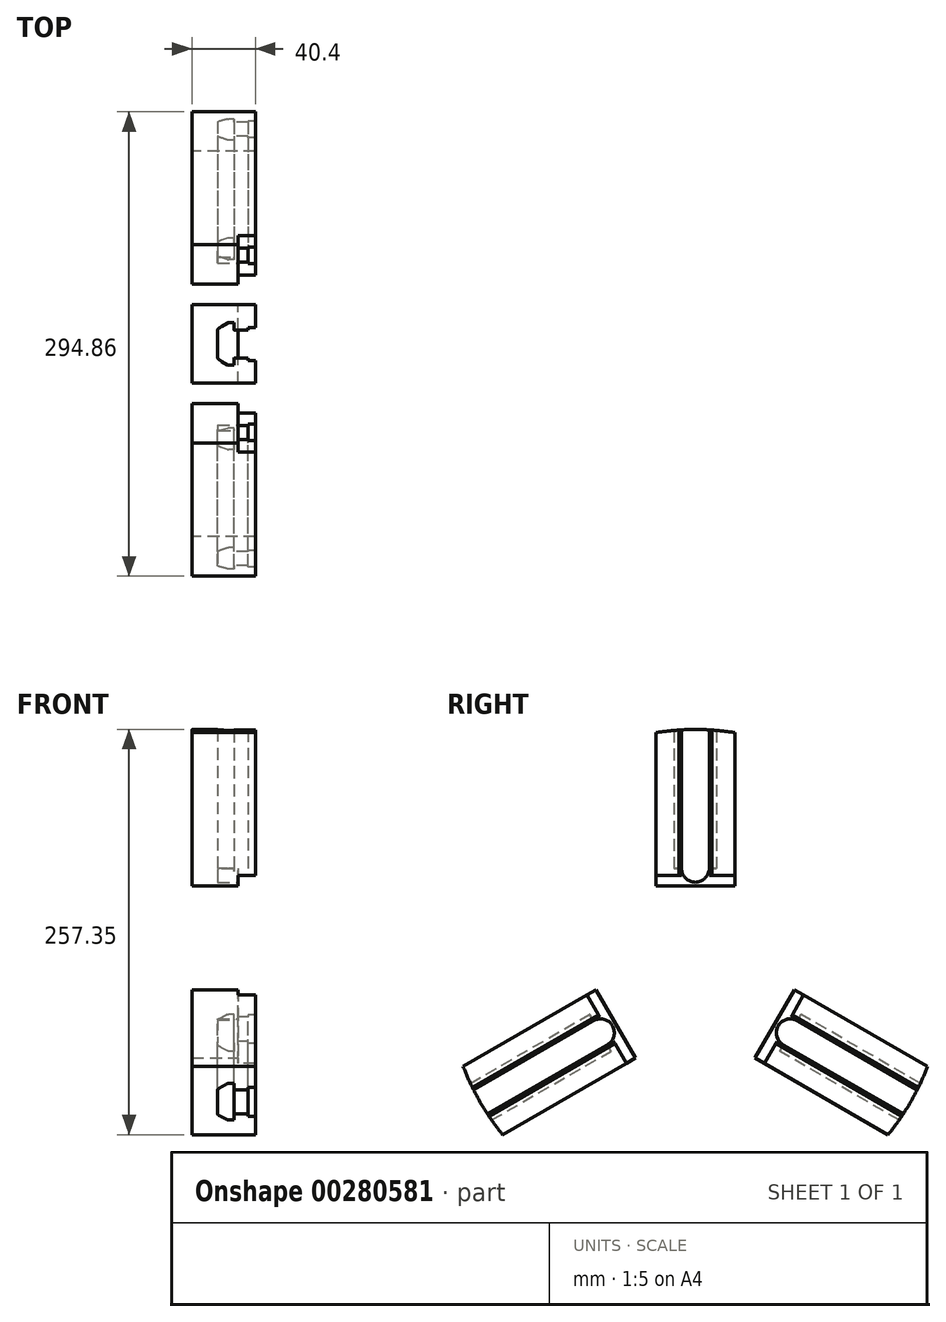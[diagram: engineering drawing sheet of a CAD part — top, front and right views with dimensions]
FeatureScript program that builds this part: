
annotation { "Feature Type Name" : "Feature", "Feature Type Description" : "" }
export const myFeature = defineFeature(function(context is Context, id is Id, definition is map)
    precondition{}
    {
        {
            var Q0;
            Q0=qCreatedBy(makeId("Right.planeOp"),FACE);
            var sketch = newSketch(context, id + "F0", { "sketchPlane" : qUnion([Q0])});
            skLineSegment(sketch, "E0", {"start": v(0, 65) * mm, "end": v(25, 65) * mm});
            skLineSegment(sketch, "E1", {"start": v(25, 65) * mm, "end": v(25, 155.8) * mm});
            skLineSegment(sketch, "E2", {"start": v(25, 155.8) * mm, "end": v(0, 155.8) * mm, "construction": true});
            skLineSegment(sketch, "E3", {"start": v(0, 155.8) * mm, "end": v(-25, 155.8) * mm, "construction": true});
            skLineSegment(sketch, "E4", {"start": v(-25, 155.8) * mm, "end": v(-25, 65) * mm});
            skLineSegment(sketch, "E5", {"start": v(-25, 65) * mm, "end": v(0, 65) * mm});
            skLineSegment(sketch, "E6", {"start": v(25, 65) * mm, "end": v(25, 58.3) * mm});
            skLineSegment(sketch, "E7", {"start": v(-25, 58.3) * mm, "end": v(-25, 65) * mm});
            skLineSegment(sketch, "E8", {"start": v(25, 58.3) * mm, "end": v(0, 58.3) * mm});
            skLineSegment(sketch, "E9", {"start": v(0, 58.3) * mm, "end": v(-25, 58.3) * mm});
            skArc(sketch, "E10", {"start": v(25, 155.8) * mm, "mid": v(0, 157.8) * mm, "end": v(-25, 155.8) * mm});
            skLineSegment(sketch, "E11.trimOffspring", {"start": v(0, 58.3) * mm, "end": v(0, 159.04) * mm, "construction": true});
            skPoint(sketch, "E12.start.orphan", {"position": v(0, 0) * mm});
            skLineSegment(sketch, "E13", {"start": v(0, 0) * mm, "end": v(0, 11) * mm, "construction": true});
            skLineSegment(sketch, "E14", {"start": v(0, 11) * mm, "end": v(0, 58.3) * mm, "construction": true});
            skSolve(sketch);
        }
        {
            var Q0;
            Q0=makeQuery(id+"F0.imprint","IMPRINT",FACE,{"disambiguationData":[TD([[makeQuery(id+"F0.imprint","IMPRINT",EDGE,{"derivedFrom":sQuery(id+"F0.wireOp",EDGE,"E0")}),1.0]])]});
            extrude(context, id + "F1", {"entities" : qUnion([Q0]), "depth" : 3 * mm, "hasSecondDirection" : true, "secondDirectionOppositeDirection" : true, "secondDirectionDepth" : 37.4 * mm});
        }
        {
            var Q0;
            Q0=makeQuery(id+"F0.imprint","IMPRINT",FACE,{"disambiguationData":[TD([[makeQuery(id+"F0.imprint","IMPRINT",EDGE,{"derivedFrom":sQuery(id+"F0.wireOp",EDGE,"E0")}),-1.0]])]});
            extrude(context, id + "F2", {"entities" : qUnion([Q0]), "operationType" : NewBodyOperationType.ADD, "oppositeDirection" : true, "depth" : 37.4 * mm, "hasSecondDirection" : true, "secondDirectionOppositeDirection" : true, "secondDirectionDepth" : 8 * mm});
        }
        {
            var Q0;
            Q0=makeQuery(id+"F1.opExtrude","SWEPT_FACE",FACE,{"disambiguationData":[OSD([sQuery(id+"F0.wireOp",EDGE,"E0"),sQuery(id+"F0.wireOp",EDGE,"E5")])]});
            var sketch = newSketch(context, id + "F3", { "sketchPlane" : qUnion([Q0])});
            skLineSegment(sketch, "E15", {"start": v(7.2, 0) * mm, "end": v(1.05, 0) * mm, "construction": true});
            skLineSegment(sketch, "E16", {"start": v(1.05, 0) * mm, "end": v(-20.37, 0) * mm, "construction": true});
            skLineSegment(sketch, "E17", {"start": v(3, 0) * mm, "end": v(3, 10.5) * mm});
            skLineSegment(sketch, "E18", {"start": v(3, 10.5) * mm, "end": v(-1.7, 10.5) * mm});
            skLineSegment(sketch, "E19", {"start": v(-1.7, 10.5) * mm, "end": v(-1.7, 8.85) * mm});
            skLineSegment(sketch, "E20", {"start": v(-1.7, 8.85) * mm, "end": v(-10.5, 8.85) * mm});
            skLineSegment(sketch, "E21", {"start": v(-10.5, 8.85) * mm, "end": v(-10.5, 13.5) * mm});
            skLineSegment(sketch, "E22", {"start": v(-10.5, 13.5) * mm, "end": v(-14.22, 13.5) * mm});
            skLineSegment(sketch, "E23", {"start": v(-14.74, 13.35) * mm, "end": v(-20.52, 9.8) * mm});
            skLineSegment(sketch, "E24", {"start": v(-21, 8.94) * mm, "end": v(-21, 0) * mm});
            skLineSegment(sketch, "E25.MirrorCS", {"start": v(3, 0) * mm, "end": v(3, -10.5) * mm});
            skLineSegment(sketch, "E26.MirrorCS", {"start": v(3, -10.5) * mm, "end": v(-1.7, -10.5) * mm});
            skLineSegment(sketch, "E27.MirrorCS", {"start": v(-1.7, -10.5) * mm, "end": v(-1.7, -8.85) * mm});
            skLineSegment(sketch, "E28.MirrorCS", {"start": v(-1.7, -8.85) * mm, "end": v(-10.5, -8.85) * mm});
            skLineSegment(sketch, "E29.MirrorCS", {"start": v(-10.5, -8.85) * mm, "end": v(-10.5, -13.5) * mm});
            skLineSegment(sketch, "E30.MirrorCS", {"start": v(-10.5, -13.5) * mm, "end": v(-14.22, -13.5) * mm});
            skLineSegment(sketch, "E31.MirrorCS", {"start": v(-14.74, -13.35) * mm, "end": v(-20.52, -9.8) * mm});
            skLineSegment(sketch, "E32.MirrorCS", {"start": v(-21, -8.94) * mm, "end": v(-21, 0) * mm});
            skPoint(sketch, "E33.visualSharp", {"position": v(-21, 9.5) * mm});
            skArc(sketch, "E33.filletArc", {"start": v(-20.52, 9.8) * mm, "mid": v(-20.87, 9.43) * mm, "end": v(-21, 8.94) * mm});
            skPoint(sketch, "E34.visualSharp", {"position": v(-21, -9.5) * mm});
            skArc(sketch, "E34.filletArc", {"start": v(-21, -8.94) * mm, "mid": v(-20.87, -9.43) * mm, "end": v(-20.52, -9.8) * mm});
            skPoint(sketch, "E35.visualSharp", {"position": v(-14.5, -13.5) * mm});
            skArc(sketch, "E35.filletArc", {"start": v(-14.74, -13.35) * mm, "mid": v(-14.49, -13.46) * mm, "end": v(-14.22, -13.5) * mm});
            skPoint(sketch, "E36.visualSharp", {"position": v(-14.5, 13.5) * mm});
            skArc(sketch, "E36.filletArc", {"start": v(-14.22, 13.5) * mm, "mid": v(-14.49, 13.46) * mm, "end": v(-14.74, 13.35) * mm});
            skPoint(sketch, "E37.visualSharp", {"position": v(-10.5, 13.5) * mm});
            skLineSegment(sketch, "E37.filletArc", {"start": v(-10.5, 13.5) * mm, "end": v(-10.5, 13.5) * mm});
            skPoint(sketch, "E38.visualSharp", {"position": v(-10.5, -13.5) * mm});
            skLineSegment(sketch, "E38.filletArc", {"start": v(-10.5, -13.5) * mm, "end": v(-10.5, -13.5) * mm});
            skLineSegment(sketch, "E39", {"start": v(-10.5, 8.85) * mm, "end": v(-10.5, -8.85) * mm});
            skSolve(sketch);
        }
        {
            var Q0;
            Q0 = qSketchRegion(id + "F3", true);
            var Q1;
            Q1=makeQuery(id+"F1.opExtrude","SWEPT_FACE",FACE,{"disambiguationData":[OSD([sQuery(id+"F0.wireOp",EDGE,"E10")])]});
            extrude(context, id + "F4", {"entities" : qUnion([Q0]), "operationType" : NewBodyOperationType.REMOVE, "endBound" : BoundingType.UP_TO_SURFACE, "oppositeDirection" : true, "endBoundEntityFace" : qUnion([Q1]), "depth" : 25 * mm});
        }
        {
            var Q0;
            Q0=makeQuery(id+"F2.opExtrude","CAP_FACE",FACE,{"disambiguationData":[OSD([sQuery(id+"F0.wireOp",EDGE,"E0"),sQuery(id+"F0.wireOp",EDGE,"E5"),sQuery(id+"F0.wireOp",EDGE,"E6"),sQuery(id+"F0.wireOp",EDGE,"E7"),sQuery(id+"F0.wireOp",EDGE,"E8"),sQuery(id+"F0.wireOp",EDGE,"E9")])],"isStart":true});
            var sketch = newSketch(context, id + "F5", { "sketchPlane" : qUnion([Q0])});
            skArc(sketch, "E40", {"start": v(-8.85, 69.65) * mm, "mid": v(0, 60.8) * mm, "end": v(8.85, 69.65) * mm});
            skLineSegment(sketch, "E41", {"start": v(0, 157.8) * mm, "end": v(8.85, 157.8) * mm});
            skLineSegment(sketch, "E42", {"start": v(0, 157.8) * mm, "end": v(-8.85, 157.8) * mm});
            skLineSegment(sketch, "E43", {"start": v(-8.85, 157.8) * mm, "end": v(-8.85, 69.65) * mm});
            skLineSegment(sketch, "E44", {"start": v(8.85, 157.8) * mm, "end": v(8.85, 69.65) * mm});
            skSolve(sketch);
        }
        {
            var Q0;
            Q0=makeQuery(id+"F4.boolean.opBoolean","COPY",FACE,{"derivedFrom":makeQuery(id+"F4.opExtrude","CAP_FACE",FACE,{"disambiguationData":[OSD([sQuery(id+"F3.wireOp",EDGE,"E17"),sQuery(id+"F3.wireOp",EDGE,"E18"),sQuery(id+"F3.wireOp",EDGE,"E19"),sQuery(id+"F3.wireOp",EDGE,"E20"),sQuery(id+"F3.wireOp",EDGE,"E21"),sQuery(id+"F3.wireOp",EDGE,"E22"),sQuery(id+"F3.wireOp",EDGE,"E23"),sQuery(id+"F3.wireOp",EDGE,"E24"),sQuery(id+"F3.wireOp",EDGE,"E25.MirrorCS"),sQuery(id+"F3.wireOp",EDGE,"E26.MirrorCS"),sQuery(id+"F3.wireOp",EDGE,"E27.MirrorCS"),sQuery(id+"F3.wireOp",EDGE,"E28.MirrorCS"),sQuery(id+"F3.wireOp",EDGE,"E29.MirrorCS"),sQuery(id+"F3.wireOp",EDGE,"E30.MirrorCS"),sQuery(id+"F3.wireOp",EDGE,"E31.MirrorCS"),sQuery(id+"F3.wireOp",EDGE,"E32.MirrorCS"),sQuery(id+"F3.wireOp",EDGE,"E33.filletArc"),sQuery(id+"F3.wireOp",EDGE,"E34.filletArc"),sQuery(id+"F3.wireOp",EDGE,"E35.filletArc"),sQuery(id+"F3.wireOp",EDGE,"E36.filletArc")])],"isStart":true})});
            extrude(context, id + "F6", {"entities" : qUnion([Q0]), "operationType" : NewBodyOperationType.ADD, "depth" : 4.7 * mm});
        }
        {
            var Q0;
            {var subQ0=sQuery(id+"F5.wireOp",EDGE,"E40");var subQ1=sQuery(id+"F0.wireOp",EDGE,"E5");var subQ2=sQuery(id+"F0.wireOp",EDGE,"E0");var subQ3=makeQuery(id+"F4.boolean.opBoolean","SPLIT",EDGE,{"disambiguationData":[topologyDisambiguationEdgeConnected([makeQuery(id+"F2.opExtrude","CAP_FACE",FACE,{"disambiguationData":[OSD([subQ2,subQ1,sQuery(id+"F0.wireOp",EDGE,"E6"),sQuery(id+"F0.wireOp",EDGE,"E7"),sQuery(id+"F0.wireOp",EDGE,"E8"),sQuery(id+"F0.wireOp",EDGE,"E9")])],"isStart":true}),makeQuery(id+"F4.opExtrude","CAP_FACE",FACE,{"disambiguationData":[OSD([sQuery(id+"F3.wireOp",EDGE,"E17"),sQuery(id+"F3.wireOp",EDGE,"E18"),sQuery(id+"F3.wireOp",EDGE,"E19"),sQuery(id+"F3.wireOp",EDGE,"E20"),sQuery(id+"F3.wireOp",EDGE,"E21"),sQuery(id+"F3.wireOp",EDGE,"E22"),sQuery(id+"F3.wireOp",EDGE,"E23"),sQuery(id+"F3.wireOp",EDGE,"E24"),sQuery(id+"F3.wireOp",EDGE,"E25.MirrorCS"),sQuery(id+"F3.wireOp",EDGE,"E26.MirrorCS"),sQuery(id+"F3.wireOp",EDGE,"E27.MirrorCS"),sQuery(id+"F3.wireOp",EDGE,"E28.MirrorCS"),sQuery(id+"F3.wireOp",EDGE,"E29.MirrorCS"),sQuery(id+"F3.wireOp",EDGE,"E30.MirrorCS"),sQuery(id+"F3.wireOp",EDGE,"E31.MirrorCS"),sQuery(id+"F3.wireOp",EDGE,"E32.MirrorCS"),sQuery(id+"F3.wireOp",EDGE,"E33.filletArc"),sQuery(id+"F3.wireOp",EDGE,"E34.filletArc"),sQuery(id+"F3.wireOp",EDGE,"E35.filletArc"),sQuery(id+"F3.wireOp",EDGE,"E36.filletArc")])],"isStart":true})])],"derivedFrom":makeQuery(id+"F2.opExtrude","CAP_EDGE",EDGE,{"disambiguationData":[OSD([subQ2,subQ1])],"isStart":true})});var subQ4=makeQuery(id+"F5.imprint","INTERSECT",VERTEX,{"disambiguationData":[OD(0.0)],"derivedFrom":[subQ3,subQ0]});Q0=makeQuery(id+"F5.imprint","IMPRINT",FACE,{"disambiguationData":[TD([[makeQuery(id+"F5.imprint","IMPRINT",EDGE,{"disambiguationData":[TD([[subQ4,-1.0]])],"derivedFrom":subQ0}),1.0]])]});}
            var Q1;
            Q1=makeQuery(id+"F5.imprint","IMPRINT",FACE,{"disambiguationData":[TD([[makeQuery(id+"F5.imprint","IMPRINT",EDGE,{"derivedFrom":sQuery(id+"F5.wireOp",EDGE,"E41")}),-1.0]])]});
            var Q2;
            Q2=makeQuery(id+"F4.boolean.opBoolean","COPY",FACE,{"derivedFrom":makeQuery(id+"F4.opExtrude","SWEPT_FACE",FACE,{"disambiguationData":[OSD([sQuery(id+"F3.wireOp",EDGE,"E24"),sQuery(id+"F3.wireOp",EDGE,"E32.MirrorCS")])]})});
            extrude(context, id + "F7", {"entities" : qUnion([Q0, Q1]), "operationType" : NewBodyOperationType.REMOVE, "endBound" : BoundingType.UP_TO_SURFACE, "oppositeDirection" : true, "endBoundEntityFace" : qUnion([Q2]), "depth" : 25 * mm});
        }
        {
            var Q0;
            Q0=makeQuery(id+"F7.boolean.opBoolean","INTERSECT",EDGE,{"derivedFrom":[makeQuery(id+"F6.opExtrude","CAP_FACE",FACE,{"disambiguationData":[OSD([sQuery(id+"F3.wireOp",EDGE,"E17"),sQuery(id+"F3.wireOp",EDGE,"E18"),sQuery(id+"F3.wireOp",EDGE,"E19"),sQuery(id+"F3.wireOp",EDGE,"E20"),sQuery(id+"F3.wireOp",EDGE,"E21"),sQuery(id+"F3.wireOp",EDGE,"E22"),sQuery(id+"F3.wireOp",EDGE,"E23"),sQuery(id+"F3.wireOp",EDGE,"E24"),sQuery(id+"F3.wireOp",EDGE,"E25.MirrorCS"),sQuery(id+"F3.wireOp",EDGE,"E26.MirrorCS"),sQuery(id+"F3.wireOp",EDGE,"E27.MirrorCS"),sQuery(id+"F3.wireOp",EDGE,"E28.MirrorCS"),sQuery(id+"F3.wireOp",EDGE,"E29.MirrorCS"),sQuery(id+"F3.wireOp",EDGE,"E30.MirrorCS"),sQuery(id+"F3.wireOp",EDGE,"E31.MirrorCS"),sQuery(id+"F3.wireOp",EDGE,"E32.MirrorCS"),sQuery(id+"F3.wireOp",EDGE,"E33.filletArc"),sQuery(id+"F3.wireOp",EDGE,"E34.filletArc"),sQuery(id+"F3.wireOp",EDGE,"E35.filletArc"),sQuery(id+"F3.wireOp",EDGE,"E36.filletArc")])],"isStart":false}),makeQuery(id+"F7.opExtrude","SWEPT_FACE",FACE,{"disambiguationData":[OSD([sQuery(id+"F5.wireOp",EDGE,"E43")])]})]});
            var Q1;
            Q1=makeQuery(id+"F7.boolean.opBoolean","INTERSECT",EDGE,{"derivedFrom":[makeQuery(id+"F6.opExtrude","CAP_FACE",FACE,{"disambiguationData":[OSD([sQuery(id+"F3.wireOp",EDGE,"E17"),sQuery(id+"F3.wireOp",EDGE,"E18"),sQuery(id+"F3.wireOp",EDGE,"E19"),sQuery(id+"F3.wireOp",EDGE,"E20"),sQuery(id+"F3.wireOp",EDGE,"E21"),sQuery(id+"F3.wireOp",EDGE,"E22"),sQuery(id+"F3.wireOp",EDGE,"E23"),sQuery(id+"F3.wireOp",EDGE,"E24"),sQuery(id+"F3.wireOp",EDGE,"E25.MirrorCS"),sQuery(id+"F3.wireOp",EDGE,"E26.MirrorCS"),sQuery(id+"F3.wireOp",EDGE,"E27.MirrorCS"),sQuery(id+"F3.wireOp",EDGE,"E28.MirrorCS"),sQuery(id+"F3.wireOp",EDGE,"E29.MirrorCS"),sQuery(id+"F3.wireOp",EDGE,"E30.MirrorCS"),sQuery(id+"F3.wireOp",EDGE,"E31.MirrorCS"),sQuery(id+"F3.wireOp",EDGE,"E32.MirrorCS"),sQuery(id+"F3.wireOp",EDGE,"E33.filletArc"),sQuery(id+"F3.wireOp",EDGE,"E34.filletArc"),sQuery(id+"F3.wireOp",EDGE,"E35.filletArc"),sQuery(id+"F3.wireOp",EDGE,"E36.filletArc")])],"isStart":false}),makeQuery(id+"F7.opExtrude","SWEPT_FACE",FACE,{"disambiguationData":[OSD([sQuery(id+"F5.wireOp",EDGE,"E44")])]})]});
            fillet(context, id + "F8", {"entities" : qUnion([Q0, Q1]), "radius" : 2.5 * mm, "tangentPropagation" : true, "allowEdgeOverflow" : false});
        }
        {
            var Q0;
            Q0=qCreatedBy(makeId("Top.planeOp"),FACE);
            var sketch = newSketch(context, id + "F9", { "sketchPlane" : qUnion([Q0])});
            skLineSegment(sketch, "E45", {"start": v(0, 0) * mm, "end": v(3.6, 0) * mm, "construction": true});
            skSolve(sketch);
        }
        {
            var Q0;
            Q0=makeQuery(id+"F1.opExtrude","SWEPT_BODY",BODY,{"disambiguationData":[OSD([sQuery(id+"F0.wireOp",EDGE,"E0"),sQuery(id+"F0.wireOp",EDGE,"E1"),sQuery(id+"F0.wireOp",EDGE,"E4"),sQuery(id+"F0.wireOp",EDGE,"E5"),sQuery(id+"F0.wireOp",EDGE,"E10")])]});
            var Q1;
            Q1=sQuery(id+"F9.wireOp",EDGE,"E45");
            circularPattern(context, id + "F10", {"entities" : qUnion([Q0]), "axis" : qUnion([Q1]), "angle" : 360 * degree, "instanceCount" : 3, "equalSpace" : true, "computeTransformsWithoutBuiltin" : true});
        }
    });
